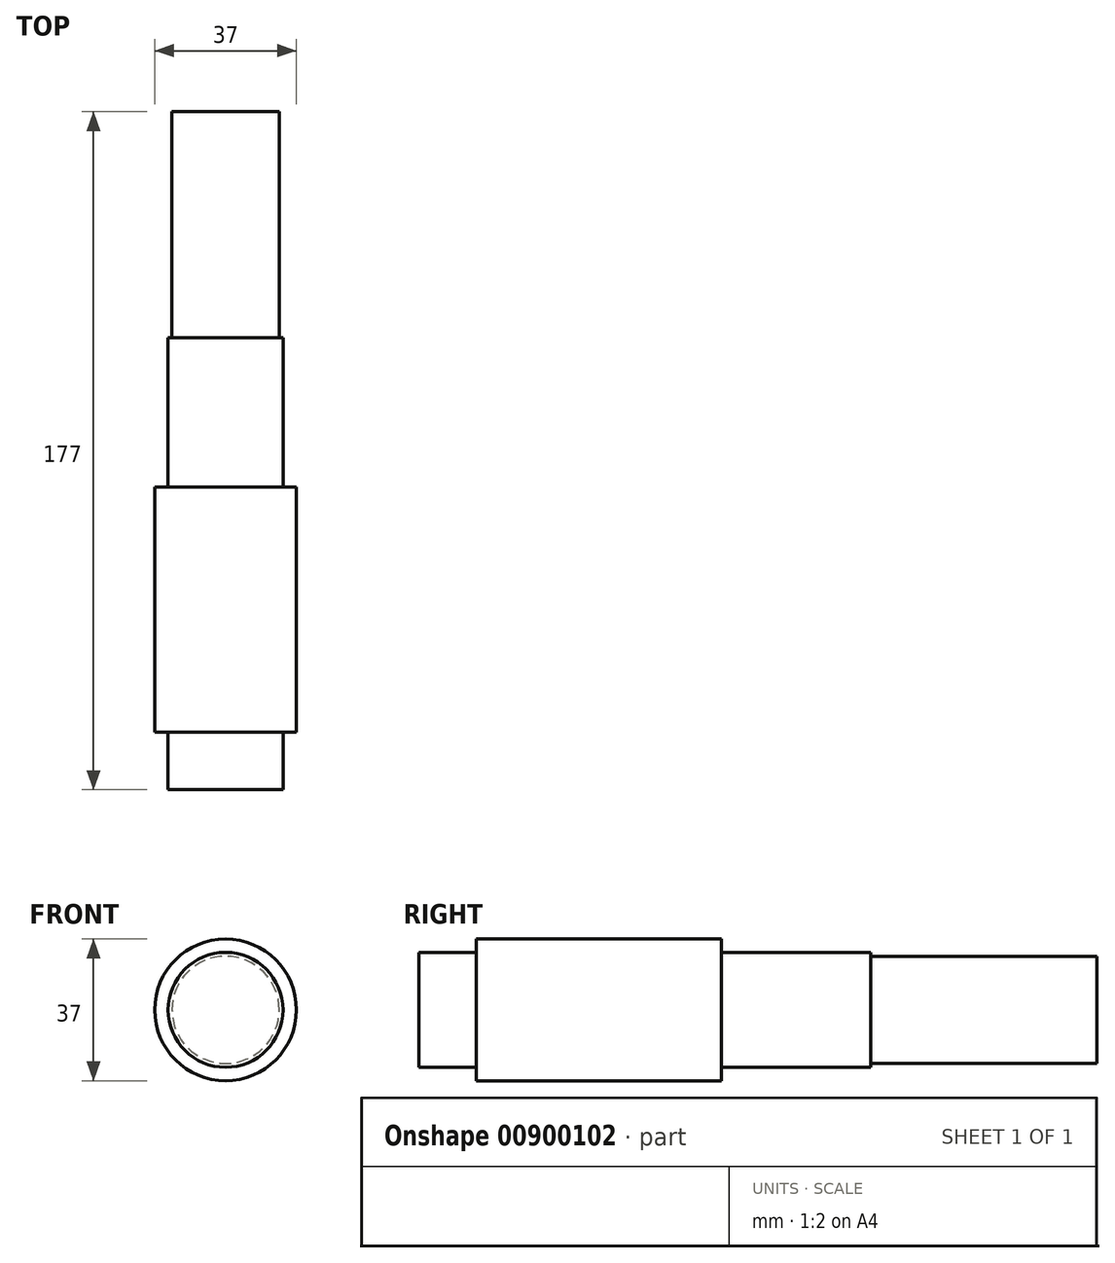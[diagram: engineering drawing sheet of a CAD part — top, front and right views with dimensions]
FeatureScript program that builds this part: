
annotation { "Feature Type Name" : "Feature", "Feature Type Description" : "" }
export const myFeature = defineFeature(function(context is Context, id is Id, definition is map)
    precondition{}
    {
        {
            var Q0;
            Q0=qCreatedBy(makeId("Front.planeOp"),FACE);
            var sketch = newSketch(context, id + "F0", { "sketchPlane" : qUnion([Q0])});
            skCircle(sketch, "E0", {"center": v(0, 0) * mm, "radius": 15 * mm});
            skSolve(sketch);
        }
        {
            var Q0;
            Q0 = qSketchRegion(id + "F0", true);
            extrude(context, id + "F1", {"entities" : qUnion([Q0]), "depth" : 15 * mm, "offsetDistance" : 25 * mm});
        }
        {
            var Q0;
            Q0=qCreatedBy(makeId("Front.planeOp"),FACE);
            var sketch = newSketch(context, id + "F2", { "sketchPlane" : qUnion([Q0])});
            skCircle(sketch, "E1", {"center": v(0, 0) * mm, "radius": 18.5 * mm});
            skSolve(sketch);
        }
        {
            var Q0;
            Q0 = qSketchRegion(id + "F2", true);
            extrude(context, id + "F3", {"entities" : qUnion([Q0]), "operationType" : NewBodyOperationType.ADD, "oppositeDirection" : true, "depth" : 64 * mm, "offsetDistance" : 25 * mm});
        }
        {
            var Q0;
            Q0=makeQuery(id+"F3.opExtrude","CAP_FACE",FACE,{"disambiguationData":[OSD([sQuery(id+"F2.wireOp",EDGE,"E1")])],"isStart":false});
            var sketch = newSketch(context, id + "F4", { "sketchPlane" : qUnion([Q0])});
            skCircle(sketch, "E2", {"center": v(0, 0) * mm, "radius": 15 * mm});
            skSolve(sketch);
        }
        {
            var Q0;
            Q0 = qSketchRegion(id + "F4", true);
            extrude(context, id + "F5", {"entities" : qUnion([Q0]), "operationType" : NewBodyOperationType.ADD, "depth" : 39 * mm, "offsetDistance" : 25 * mm});
        }
        {
            var Q0;
            Q0=makeQuery(id+"F5.opExtrude","CAP_FACE",FACE,{"disambiguationData":[OSD([sQuery(id+"F4.wireOp",EDGE,"E2")])],"isStart":false});
            var sketch = newSketch(context, id + "F6", { "sketchPlane" : qUnion([Q0])});
            skCircle(sketch, "E3", {"center": v(0, 0) * mm, "radius": 14 * mm});
            skSolve(sketch);
        }
        {
            var Q0;
            Q0 = qSketchRegion(id + "F6", true);
            extrude(context, id + "F7", {"entities" : qUnion([Q0]), "operationType" : NewBodyOperationType.ADD, "depth" : 59 * mm, "offsetDistance" : 25 * mm});
        }
    });
